# Revit family: Interceptor_Grease-Zurn-Z1174
name_source: partatom
category: Plumbing Fixtures
units: mm (PartAtom-declared; Revit-internal decimal feet)

## family parameters
Always vertical = Yes
Cut with Voids When Loaded = No
Maintain Annotation Orientation = No
OmniClass Number = 23.45.30.00
OmniClass Title = Washing and Waste Disposal Equipment
Part Type = Normal
Room Calculation Point = No
Round Connector Dimension = Use Radius
Shared = No
Work Plane-Based = No

## types (16) — shared parameters
Air Intake Vent Radius = 0.375 "
Assembly Code = D2090300
CW Connection = No
Default Elevation = 20 "
Description = GREASE INTERCEPTOR WITH Z1183 SOLIDS INTERCEPTOR COMBINATION AND GREASE EATING BACTERIA DOSING UNIT
Flow Controller = Iron - Zurn - Cast - Painted - Blue
HW Connection = No
Manufacturer = Zurn Water, LLC
Manufacurer Brand = Zurn
Modified Date = 02/03/2026
Product Documentation Link = https://files.zurn.com
Product Page URL = https://www.zurn.com
Product data url = https://www.bimobject.com
URL = www.zurn.com
Vent Connection = Yes
WFU = 1
Waste Connection = Yes
zero-valued in all types: CWFU, HWFU

## per-type parameters (varying)
| type | Approx. Weight (Lbs) | Connector Radius | Dim C | Dim D/E | Dim F | Dim G | Dim H | Flow Rate (GPM) | Grease Capacity | Main Material | Model | Pipe Size_A Inside Diameter | Pipe Size_A Nominal Diameter | Pipe Size_A Outer Diameter | Type Comments | Water Capacity |
| Z1174-100-4 | 60.00 lb | 1 " | 10 " | 7.25 " | 20.375 " | 9.875 " | 9.875 " | 4 GPM | 8.00 lb | Steel - Zurn - Stainless - A.R.E Coated - Type - 304 | Z1174 | 2.067 " | 2 " | 2.375 " | Z1174-200-7 GPM with 2 Inch Inlet/ outlet. | 3.0 gal |
| Z1174-200-7 | 76.00 lb | 1 " | 11.25 " | 8.125 " | 21.75 " | 11.875 " | 11.875 " | 7 GPM | 14.00 lb | Steel - Zurn - Stainless - A.R.E Coated - Type - 304 | Z1174 | 2.067 " | 2 " | 2.375 " | Z1174-200-7 GPM with 2 Inch Inlet/ outlet. | 5.0 gal |
| Z1174-300-10 | 93.00 lb | 1 " | 11.75 " | 8.25 " | 25.125 " | 14 " | 14 " | 10 GPM | 20.00 lb | Steel - Zurn - Stainless - A.R.E Coated - Type - 304 | Z1174 | 2.067 " | 2 " | 2.375 " | Z1174-300-10 GPM with 2 Inch Inlet/ outlet. | 6.0 gal |
| Z1174-400-15 | 116.00 lb | 1.5 " | 13.375 " | 9.375 " | 27.125 " | 16.75 " | 16.75 " | 15 GPM | 30.00 lb | Steel - Zurn - Stainless - A.R.E Coated - Type - 304 | Z1174 | 3.068 " | 3 " | 3.5 " | Z1174-400-15 GPM with 3 Inch Inlet/ outlet. | 10.0 gal |
| Z1174-500-20 | 136.00 lb | 1.5 " | 15 " | 11.75 " | 30 " | 17.25 " | 17.25 " | 20 GPM | 40.00 lb | Steel - Zurn - Stainless - A.R.E Coated - Type - 304 | Z1174 | 3.068 " | 3 " | 3.5 " | Z1174-500-20 GPM with 3 Inch Inlet/ outlet. | 16.0 gal |
| Z1174-600-25 | 169.00 lb | 1.5 " | 17 " | 12.5 " | 32.25 " | 19.875 " | 19.875 " | 25 GPM | 50.00 lb | Steel - Zurn - Stainless - A.R.E Coated - Type - 304 | Z1174 | 3.068 " | 3 " | 3.5 " | Z1174-600-25 GPM with 3 Inch Inlet/ outlet. | 21.0 gal |
| Z1174-700-35 | 209.00 lb | 1.5 " | 18.75 " | 14.25 " | 34.125 " | 22.5 " | 22.5 " | 35 GPM | 70.00 lb | Steel - Zurn - Stainless - A.R.E Coated - Type - 304 | Z1174 | 3.068 " | 3 " | 3.5 " | Z1174-700-35 GPM with 3 Inch Inlet/ outlet. | 30.0 gal |
| Z1174-800-50 | 239.00 lb | 1.5 " | 21.5 " | 16 " | 36 " | 24.5 " | 24.5 " | 50 GPM | 100.00 lb | Steel - Zurn - Stainless - A.R.E Coated - Type - 304 | Z1174 | 3.068 " | 3 " | 3.5 " | Z1174-800-50 GPM with 3 Inch Inlet/ outlet. | 40.0 gal |
| ZS1174-100-4 | 60.00 lb | 1 " | 10 " | 7.25 " | 20.375 " | 9.875 " | 9.875 " | 4 GPM | 8.00 lb | Steel - Zurn - Stainless - Type - 304 | Z1174 | 2.067 " | 2 " | 2.375 " | Z1174-200-7 GPM with 2 Inch Inlet/ outlet. | 3.0 gal |
| ZS1174-200-7 | 76.00 lb | 1 " | 11.25 " | 8.125 " | 21.75 " | 11.875 " | 11.875 " | 7 GPM | 14.00 lb | Steel - Zurn - Stainless - Type - 304 | ZS1174 | 2.067 " | 2 " | 2.375 " | ZSS1174-200-7 GPM with 2 Inch Inlet/ outlet. | 5.0 gal |
| ZS1174-300-10 | 93.00 lb | 1 " | 11.75 " | 8.25 " | 25.125 " | 14 " | 14 " | 10 GPM | 20.00 lb | Steel - Zurn - Stainless - Type - 304 | ZS1174 | 2.067 " | 2 " | 2.375 " | ZS1174-300-10 GPM with 2 Inch Inlet/ outlet. | 6.0 gal |
| ZS1174-400-15 | 116.00 lb | 1.5 " | 13.375 " | 9.375 " | 27.125 " | 16.75 " | 16.75 " | 15 GPM | 30.00 lb | Steel - Zurn - Stainless - Type - 304 | ZS1174 | 3.068 " | 3 " | 3.5 " | ZS1174-400-15 GPM with 3 Inch Inlet/ outlet. | 10.0 gal |
| ZS1174-500-20 | 136.00 lb | 1.5 " | 15 " | 11.75 " | 30 " | 17.25 " | 17.25 " | 20 GPM | 40.00 lb | Steel - Zurn - Stainless - Type - 304 | ZS1174 | 3.068 " | 3 " | 3.5 " | ZS1174-500-20 GPM with 3 Inch Inlet/ outlet. | 16.0 gal |
| ZS1174-600-25 | 169.00 lb | 1.5 " | 17 " | 12.5 " | 32.25 " | 19.875 " | 19.875 " | 25 GPM | 50.00 lb | Steel - Zurn - Stainless - Type - 304 | ZS1174 | 3.068 " | 3 " | 3.5 " | ZS1174-600-25 GPM with 3 Inch Inlet/ outlet. | 21.0 gal |
| ZS1174-700-35 | 209.00 lb | 1.5 " | 18.75 " | 14.25 " | 34.125 " | 22.5 " | 22.5 " | 35 GPM | 70.00 lb | Steel - Zurn - Stainless - Type - 304 | ZS1174 | 3.068 " | 3 " | 3.5 " | ZS1174-700-35 GPM with 3 Inch Inlet/ outlet. | 30.0 gal |
| ZS1174-800-50 | 239.00 lb | 1.5 " | 21.5 " | 16 " | 36 " | 24.5 " | 24.5 " | 50 GPM | 100.00 lb | Steel - Zurn - Stainless - Type - 304 | ZS1174 | 3.068 " | 3 " | 3.5 " | ZS1174-800-50 GPM with 3 Inch Inlet/ outlet. | 40.0 gal |

## geometry (parser evidence)
native form markers: Sweep x2
no freeform markers — native parametric forms only
